FREECAD ASSEMBLY — COMPONENT RECIPES ("EL-Load-Case1")

This assembly document has 14 components, labeled P0..P13 below (a component is one placed body or linked part). 3 of them carry a construction recipe — the FreeCAD feature program that regenerates the part from scratch, quoted from this document or its linked companion documents; the rest are supplied as boundary geometry only. No exploded tour is included for this assembly.
COMPONENT P0 — geometry summary ("EL-Load-Analog"; no construction recipe available for this part):
  bounding box: 188.2 x 95.0 x 51.8 mm
  tessellated surface: 174,292 triangles
  volume: 45099 mm^3 (5% of its bounding box)
COMPONENT P1 — geometry summary ("EL-Load-Analog001"; no construction recipe available for this part):
  bounding box: 185.0 x 95.0 x 41.1 mm
  tessellated surface: 106,424 triangles
  volume: 35915 mm^3 (5% of its bounding box)
COMPONENT P2 — geometry summary ("EL-Load-PowerTest2"; no construction recipe available for this part):
  bounding box: 169.3 x 72.5 x 20.0 mm
  tessellated surface: 158,708 triangles
  volume: 24229 mm^3 (10% of its bounding box)
COMPONENT P3 — geometry summary ("EL-Load-PowerTest003"; no construction recipe available for this part):
  bounding box: 170.0 x 72.5 x 20.0 mm
  tessellated surface: 159,136 triangles
  volume: 23743 mm^3 (10% of its bounding box)
COMPONENT P4 — geometry summary ("EL-Load-PowerTest004"; no construction recipe available for this part):
  bounding box: 175.0 x 72.5 x 20.0 mm
  tessellated surface: 159,700 triangles
  volume: 25175 mm^3 (10% of its bounding box)
COMPONENT P5 — geometry summary ("EL-Load-Panel"; no construction recipe available for this part):
  bounding box: 118.0 x 45.0 x 37.4 mm
  tessellated surface: 35,930 triangles
  volume: 9733 mm^3 (5% of its bounding box)
COMPONENT P6 — geometry summary ("EL-Load-Panel003"; no construction recipe available for this part):
  bounding box: 127.0 x 53.0 x 37.4 mm
  tessellated surface: 37,466 triangles
  volume: 11392 mm^3 (5% of its bounding box)
COMPONENT P7 — geometry summary ("EL-Load-Panel005"; no construction recipe available for this part):
  bounding box: 127.0 x 53.0 x 37.4 mm
  tessellated surface: 53,262 triangles
  volume: 10742 mm^3 (4% of its bounding box)
COMPONENT P8 — geometry summary ("EL-Load-Panel006"; no construction recipe available for this part):
  bounding box: 127.0 x 53.0 x 37.4 mm
  tessellated surface: 53,262 triangles
  volume: 10742 mm^3 (4% of its bounding box)
COMPONENT P9 — geometry summary ("EL-Load-Power-MCU"; no construction recipe available for this part):
  bounding box: 179.0 x 72.5 x 19.1 mm
  tessellated surface: 186,564 triangles
  volume: 26376 mm^3 (11% of its bounding box)
COMPONENT P10 — recipe-attached ("Heatsink", modeled in this document).
Construction recipe (the document's own serialized feature program — sketch geometry with constraints, then the solid features built on it; lengths are millimeters unless a unit is written):

FEATURE [PartDesign::SubShapeBinder] Binder
  BindCopyOnChange = 0
  BindMode = 0
  ClaimChildren = false
  Context = -> Body [Binder.]
  Fuse = false
  MakeFace = true
  OffsetFill = false
  OffsetIntersection = false
  OffsetJoinType = 0
  OffsetOpenResult = false
  PartialLoad = false
  Relative = true
  Support = -> [Shape125[Face11]]
  _Version = 2
FEATURE [PartDesign::Pad] Pad
  Direction = (1,0,1e-16)
  Length = 140
  Length2 = 10
  Profile = -> Binder
  Type = 0
FEATURE [PartDesign::Body] Body  label="Heatsink"
  Group = -> [Binder,Pad]
  Origin = -> Origin067
  Tip = -> Pad
COMPONENT P11 — recipe-attached ("PCBFrame1", modeled in this document).
Construction recipe (the document's own serialized feature program — sketch geometry with constraints, then the solid features built on it; lengths are millimeters unless a unit is written):

FEATURE [Sketcher::SketchObject] Sketch
  FullyConstrained = false
  MapMode = 5
  Support = -> [XY_Plane068]
  sketch-geometry (72):
    g0: LineSegment StartX=12.25 StartY=182 StartZ=0 EndX=190.25 EndY=182 EndZ=0
    g1: LineSegment StartX=196.25 StartY=176 StartZ=0 EndX=196.25 EndY=3 EndZ=0
    g2: LineSegment StartX=190.25 StartY=-3 StartZ=0 EndX=12.25 EndY=-3 EndZ=0
    g3: LineSegment StartX=6.25 StartY=3 StartZ=0 EndX=6.25 EndY=97 EndZ=0
    g4: ArcOfCircle CenterX=190.25 CenterY=176 CenterZ=0 NormalX=0 NormalY=0 NormalZ=1 AngleXU=0 Radius=6 StartAngle=1.2e-15 EndAngle=1.5708
    g5: GeomPoint X=196.25 Y=182 Z=0
    g6: ArcOfCircle CenterX=190.25 CenterY=3 CenterZ=0 NormalX=0 NormalY=0 NormalZ=1 AngleXU=0 Radius=6 StartAngle=4.71239 EndAngle=6.28319
    g7: GeomPoint X=196.25 Y=-3 Z=0
    g8: ArcOfCircle CenterX=12.25 CenterY=176 CenterZ=0 NormalX=0 NormalY=0 NormalZ=1 AngleXU=0 Radius=6 StartAngle=1.5708 EndAngle=3.14159
    g9: GeomPoint X=6.25 Y=182 Z=0
    g10: ArcOfCircle CenterX=12.25 CenterY=3 CenterZ=0 NormalX=0 NormalY=0 NormalZ=1 AngleXU=0 Radius=6 StartAngle=3.14159 EndAngle=4.71239
    g11: GeomPoint X=6.25 Y=-3 Z=0
    g12: Circle CenterX=11 CenterY=173.498 CenterZ=0 NormalX=0 NormalY=0 NormalZ=1 AngleXU=0 Radius=1.45
    g13: Circle CenterX=11 CenterY=89.4976 CenterZ=0 NormalX=0 NormalY=0 NormalZ=1 AngleXU=0 Radius=1.45
    g14: Circle CenterX=180.742 CenterY=173.605 CenterZ=0 NormalX=0 NormalY=0 NormalZ=1 AngleXU=0 Radius=1.45
    g15: Circle CenterX=181.761 CenterY=91.0561 CenterZ=0 NormalX=0 NormalY=0 NormalZ=1 AngleXU=0 Radius=1.45
    g16: ArcOfCircle CenterX=48.25 CenterY=97.4976 CenterZ=0 NormalX=0 NormalY=0 NormalZ=1 AngleXU=0 Radius=8 StartAngle=3.14159 EndAngle=4.71239
    g17: LineSegment StartX=40.25 StartY=97.4976 StartZ=0 EndX=40.25 EndY=122 EndZ=0
    g18: ArcOfCircle CenterX=48.25 CenterY=122 CenterZ=0 NormalX=0 NormalY=0 NormalZ=1 AngleXU=0 Radius=8 StartAngle=1.5708 EndAngle=3.14159
    g19: LineSegment StartX=48.25 StartY=130 StartZ=0 EndX=168.625 EndY=130 EndZ=0
    g20: ArcOfCircle CenterX=168.625 CenterY=122 CenterZ=0 NormalX=0 NormalY=0 NormalZ=1 AngleXU=0 Radius=8 StartAngle=-9e-16 EndAngle=1.5708
    g21: LineSegment StartX=176.625 StartY=122 StartZ=0 EndX=176.625 EndY=97.4976 EndZ=0
    g22: ArcOfCircle CenterX=168.625 CenterY=97.4976 CenterZ=0 NormalX=0 NormalY=0 NormalZ=1 AngleXU=0 Radius=8 StartAngle=4.71239 EndAngle=6.28319
    g23: LineSegment StartX=168.625 StartY=89.4976 StartZ=0 EndX=48.25 EndY=89.4976 EndZ=0
    g24: GeomPoint X=40.25 Y=89.4976 Z=0
    g25: GeomPoint X=176.625 Y=130 Z=0
    g26: ArcOfCircle CenterX=23.25 CenterY=147 CenterZ=0 NormalX=0 NormalY=0 NormalZ=1 AngleXU=0 Radius=8 StartAngle=3.14159 EndAngle=4.71239
    g27: LineSegment StartX=15.25 StartY=147 StartZ=0 EndX=15.25 EndY=165.498 EndZ=0
    g28: ArcOfCircle CenterX=23.25 CenterY=165.498 CenterZ=0 NormalX=0 NormalY=0 NormalZ=1 AngleXU=0 Radius=8 StartAngle=1.5708 EndAngle=3.14159
    g29: LineSegment StartX=23.25 StartY=173.498 StartZ=0 EndX=168.564 EndY=173.498 EndZ=0
    g30: ArcOfCircle CenterX=168.564 CenterY=165.498 CenterZ=0 NormalX=0 NormalY=0 NormalZ=1 AngleXU=0 Radius=8 StartAngle=-1.8e-15 EndAngle=1.5708
    g31: LineSegment StartX=176.564 StartY=165.498 StartZ=0 EndX=176.564 EndY=147 EndZ=0
    g32: ArcOfCircle CenterX=168.564 CenterY=147 CenterZ=0 NormalX=0 NormalY=0 NormalZ=1 AngleXU=0 Radius=8 StartAngle=4.71239 EndAngle=6.28319
    g33: LineSegment StartX=168.564 StartY=139 StartZ=0 EndX=23.25 EndY=139 EndZ=0
    g34: GeomPoint X=15.25 Y=139 Z=0
    g35: GeomPoint X=176.564 Y=173.498 Z=0
    g36: LineSegment StartX=6.25 StartY=130 StartZ=0 EndX=23.25 EndY=130 EndZ=0
    g37: ArcOfCircle CenterX=23.25 CenterY=122 CenterZ=0 NormalX=0 NormalY=0 NormalZ=1 AngleXU=0 Radius=8 StartAngle=-9e-16 EndAngle=1.5708
    g38: LineSegment StartX=31.25 StartY=122 StartZ=0 EndX=31.25 EndY=105 EndZ=0
    g39: ArcOfCircle CenterX=23.25 CenterY=105 CenterZ=0 NormalX=0 NormalY=0 NormalZ=1 AngleXU=0 Radius=8 StartAngle=4.71239 EndAngle=6.28319
    g40: LineSegment StartX=23.25 StartY=97 StartZ=0 EndX=6.25 EndY=97 EndZ=0
    g41: GeomPoint X=-2.4437 Y=97 Z=0
    g42: GeomPoint X=31.25 Y=130 Z=0
    g43: LineSegment StartX=6.25 StartY=130 StartZ=0 EndX=6.25 EndY=176 EndZ=0
    g44: LineSegment StartX=15.25 StartY=147 StartZ=0 EndX=6.25 EndY=147 EndZ=0
    g45: LineSegment StartX=11 StartY=173.498 StartZ=0 EndX=16.5518 EndY=169.872 EndZ=0
    g46: LineSegment StartX=180.742 StartY=173.605 StartZ=0 EndX=175.223 EndY=169.931 EndZ=0
    g47: LineSegment StartX=181.761 StartY=91.0561 StartZ=0 EndX=175.807 EndY=93.9755 EndZ=0
    g48: LineSegment StartX=23.25 StartY=130 StartZ=0 EndX=23.25 EndY=139 EndZ=0
    g49: LineSegment StartX=48.25 StartY=130 StartZ=0 EndX=48.25 EndY=139 EndZ=0
    g50: LineSegment StartX=31.25 StartY=105 StartZ=0 EndX=40.25 EndY=105 EndZ=0
    g51: Circle CenterX=24.67 CenterY=76.67 CenterZ=0 NormalX=0 NormalY=0 NormalZ=1 AngleXU=0 Radius=1.45
    g52: Circle CenterX=24.67 CenterY=24.67 CenterZ=0 NormalX=0 NormalY=0 NormalZ=1 AngleXU=0 Radius=1.45
    g53: Circle CenterX=191.67 CenterY=24.67 CenterZ=0 NormalX=0 NormalY=0 NormalZ=1 AngleXU=0 Radius=1.45
    g54: Circle CenterX=191.67 CenterY=76.67 CenterZ=0 NormalX=0 NormalY=0 NormalZ=1 AngleXU=0 Radius=1.45
    g55: LineSegment StartX=24.67 StartY=24.67 StartZ=0 EndX=191.67 EndY=24.67 EndZ=0
    g56: LineSegment StartX=191.67 StartY=24.67 StartZ=0 EndX=191.67 EndY=76.67 EndZ=0
    g57: LineSegment StartX=191.67 StartY=76.67 StartZ=0 EndX=24.67 EndY=76.67 EndZ=0
    g58: LineSegment StartX=24.67 StartY=76.67 StartZ=0 EndX=24.67 EndY=24.67 EndZ=0
    g59: ArcOfCircle CenterX=36.92 CenterY=14 CenterZ=0 NormalX=0 NormalY=0 NormalZ=1 AngleXU=0 Radius=8 StartAngle=3.14159 EndAngle=4.71239
    g60: LineSegment StartX=28.92 StartY=14 StartZ=0 EndX=28.92 EndY=68.67 EndZ=0
    g61: ArcOfCircle CenterX=36.92 CenterY=68.67 CenterZ=0 NormalX=0 NormalY=0 NormalZ=1 AngleXU=0 Radius=8 StartAngle=1.5708 EndAngle=3.14159
    g62: LineSegment StartX=36.92 StartY=76.67 StartZ=0 EndX=179.42 EndY=76.67 EndZ=0
    g63: ArcOfCircle CenterX=179.42 CenterY=68.67 CenterZ=0 NormalX=0 NormalY=0 NormalZ=1 AngleXU=0 Radius=8 StartAngle=-9e-16 EndAngle=1.5708
    g64: LineSegment StartX=187.42 StartY=68.67 StartZ=0 EndX=187.42 EndY=14 EndZ=0
    g65: ArcOfCircle CenterX=179.42 CenterY=14 CenterZ=0 NormalX=0 NormalY=0 NormalZ=1 AngleXU=0 Radius=8 StartAngle=4.71239 EndAngle=6.28319
    g66: LineSegment StartX=179.42 StartY=6 StartZ=0 EndX=36.92 EndY=6 EndZ=0
    g67: GeomPoint X=28.92 Y=6 Z=0
    g68: GeomPoint X=187.42 Y=76.67 Z=0
    g69: LineSegment StartX=36.92 StartY=6 StartZ=0 EndX=36.92 EndY=-3 EndZ=0
    g70: LineSegment StartX=24.67 StartY=76.67 StartZ=0 EndX=30.2218 EndY=73.0443 EndZ=0
    g71: LineSegment StartX=191.67 StartY=76.67 StartZ=0 EndX=186.118 EndY=73.0443 EndZ=0
  constraints (180):
    c: Horizontal(g0)
    c: Horizontal(g2)
    c: Vertical(g1)
    c: Vertical(g3)
    c: DistanceY(g11,g9) = 185
    c: DistanceY(g11,g-1) = 3
    c: DistanceX(g-1,g11) = 6.25
    c: DistanceX(g9,g5) = 190
    c: PointOnObject(g5,g0)
    c: PointOnObject(g5,g1)
    c: Tangent(g0,g4) = 1.5708
    c: Tangent(g1,g4) = 1.5708
    c: PointOnObject(g7,g1)
    c: PointOnObject(g7,g2)
    c: Tangent(g1,g6) = 1.5708
    c: Tangent(g2,g6) = 1.5708
    c: PointOnObject(g9,g0)
    c: PointOnObject(g9,g3)
    c: Tangent(g0,g8) = 1.5708
    c: PointOnObject(g11,g2)
    c: PointOnObject(g11,g3)
    c: Tangent(g2,g10) = 1.5708
    c: Tangent(g3,g10) = 1.5708
    c: Equal(g10,g8)
    c: Equal(g8,g4)
    c: Equal(g4,g6)
    c: Radius(g4) = 6
    c: Equal(g15,g14)
    c: Equal(g14,g12)
    c: Equal(g12,g13)
    c: Vertical(g12,g13)
    c: Diameter(g15) = 2.9
    c: DistanceX(g15) = 181.761
    c: DistanceY(g15) = 91.0561
    c: DistanceX(g14) = 180.742
    c: DistanceY(g14) = 173.605
    c: DistanceX(g12) = 11
    c: DistanceY(g12) = 173.498
    c: DistanceY(g13,g12) = 84
    c: Tangent(g16,g17) = 1.5708
    c: Tangent(g17,g18) = 1.5708
    c: Tangent(g18,g19) = 1.5708
    c: Tangent(g19,g20) = 1.5708
    c: Tangent(g20,g21) = 1.5708
    c: Tangent(g21,g22) = 1.5708
    c: Tangent(g22,g23) = 1.5708
    c: Tangent(g23,g16) = 1.5708
    c: Horizontal(g19)
    c: Horizontal(g23)
    c: Vertical(g17)
    c: Vertical(g21)
    c: Equal(g16,g18)
    c: Equal(g18,g20)
    c: Equal(g20,g22)
    c: PointOnObject(g24,g17)
    c: PointOnObject(g24,g23)
    c: PointOnObject(g25,g19)
    c: PointOnObject(g25,g21)
    c: Tangent(g26,g27) = 1.5708
    c: Tangent(g27,g28) = 1.5708
    c: Tangent(g28,g29) = 1.5708
    c: Tangent(g29,g30) = 1.5708
    c: Tangent(g30,g31) = 1.5708
    c: Tangent(g31,g32) = 1.5708
    c: Tangent(g32,g33) = 1.5708
    c: Tangent(g33,g26) = 1.5708
    c: Horizontal(g29)
    c: Horizontal(g33)
    c: Vertical(g27)
    c: Vertical(g31)
    c: Equal(g26,g28)
    c: Equal(g28,g30)
    c: Equal(g30,g32)
    c: PointOnObject(g34,g27)
    c: PointOnObject(g34,g33)
    c: PointOnObject(g35,g29)
    c: PointOnObject(g35,g31)
    c: Tangent(g36,g37) = 1.5708
    c: Tangent(g37,g38) = 1.5708
    c: Tangent(g38,g39) = 1.5708
    c: Tangent(g39,g40) = 1.5708
    c: Horizontal(g36)
    c: Horizontal(g40)
    c: Vertical(g38)
    c: Equal(g37,g39)
    c: PointOnObject(g41,g40)
    c: PointOnObject(g42,g36)
    c: PointOnObject(g42,g38)
    c: Coincident(g3,g40)
    c: Coincident(g43,g36)
    c: Equal(g18,g37)
    c: Equal(g37,g26)
    c: Horizontal(g28,g12)
    c: Coincident(g44,g26)
    c: Horizontal(g44)
    c: Coincident(g45,g12)
    c: PointOnObject(g45,g28)
    c: Perpendicular(g28,g45)
    c: Coincident(g46,g14)
    c: PointOnObject(g46,g30)
    c: Perpendicular(g30,g46)
    c: Equal(g46,g45)
    c: Perpendicular(g22,g47)
    c: Equal(g47,g46)
    c: PointOnObject(g47,g22)
    c: Coincident(g47,g15)
    c: Vertical(g43)
    c: PointOnObject(g44,g43)
    c: Radius(g26) = 8
    c: Vertical(g36,g3)
    c: DistanceY(g36,g0) = 52
    c: DistanceY(g3,g36) = 33
    c: Coincident(g48,g36)
    c: Coincident(g48,g26)
    c: Vertical(g48)
    c: Equal(g48,g44)
    c: Horizontal(g16,g13)
    c: Coincident(g49,g18)
    c: PointOnObject(g49,g33)
    c: Vertical(g49)
    c: Coincident(g50,g38)
    c: PointOnObject(g50,g17)
    c: Horizontal(g50)
    c: Equal(g49,g48)
    c: Equal(g50,g48)
    c: DistanceX(g3,g38) = 25
    c: Tangent(g43,g8) = 1.5708
    c: Equal(g54,g53)
    c: Equal(g53,g52)
    c: Equal(g52,g51)
    c: Equal(g51,g15)
    c: Coincident(g55,g56)
    c: Coincident(g56,g57)
    c: Coincident(g57,g58)
    c: Coincident(g58,g55)
    c: Horizontal(g55)
    c: Horizontal(g57)
    c: Vertical(g56)
    c: Vertical(g58)
    c: Coincident(g52,g55)
    c: Coincident(g54,g56)
    c: Coincident(g55,g53)
    c: Coincident(g57,g51)
    c: DistanceY(g58,g58) = 52
    c: DistanceX(g52,g53) = 167
    c: DistanceX(g52) = 24.67
    c: DistanceY(g52) = 24.67
    c: Tangent(g59,g60) = 1.5708
    c: Tangent(g60,g61) = 1.5708
    c: Tangent(g61,g62) = 1.5708
    c: Tangent(g62,g63) = 1.5708
    c: Tangent(g63,g64) = 1.5708
    c: Tangent(g64,g65) = 1.5708
    c: Tangent(g65,g66) = 1.5708
    c: Tangent(g66,g59) = 1.5708
    c: Horizontal(g62)
    c: Horizontal(g66)
    c: Vertical(g60)
    c: Vertical(g64)
    c: Equal(g59,g61)
    c: Equal(g61,g63)
    c: Equal(g63,g65)
    c: PointOnObject(g67,g60)
    c: PointOnObject(g67,g66)
    c: PointOnObject(g68,g62)
    c: PointOnObject(g68,g64)
    c: Equal(g61,g16)
    c: Horizontal(g61,g51)
    c: Coincident(g69,g59)
    c: PointOnObject(g69,g2)
    c: Vertical(g69)
    c: Coincident(g70,g51)
    c: PointOnObject(g70,g61)
    c: Perpendicular(g61,g70)
    c: Equal(g69,g50)
    c: Equal(g70,g45)
    c: Coincident(g71,g54)
    c: PointOnObject(g71,g63)
    c: Perpendicular(g63,g71)
    c: Equal(g71,g70)
FEATURE [PartDesign::Pad] Pad001
  Direction = (0,0,1)
  Length = 1.6
  Length2 = 10
  Profile = -> Sketch
  ReferenceAxis = -> Sketch [N_Axis]
  Reversed = true
  Type = 0
FEATURE [Sketcher::SketchObject] Sketch001
  ExternalGeometry = -> [Pad001]
  FullyConstrained = true
  MapMode = 5
  Support = -> [XY_Plane068]
  sketch-geometry (12):
    g0: Circle CenterX=24.67 CenterY=24.67 CenterZ=0 NormalX=0 NormalY=0 NormalZ=1 AngleXU=0 Radius=1.45
    g1: Circle CenterX=191.67 CenterY=76.67 CenterZ=0 NormalX=0 NormalY=0 NormalZ=1 AngleXU=0 Radius=1.45
    g2: Circle CenterX=191.67 CenterY=24.67 CenterZ=0 NormalX=0 NormalY=0 NormalZ=1 AngleXU=0 Radius=1.45
    g3: ArcOfCircle CenterX=24.67 CenterY=76.67 CenterZ=0 NormalX=0 NormalY=0 NormalZ=1 AngleXU=0 Radius=4.25 StartAngle=-4.361e-13 EndAngle=3.14159
    g4: ArcOfCircle CenterX=24.67 CenterY=6 CenterZ=0 NormalX=0 NormalY=0 NormalZ=1 AngleXU=0 Radius=4.25 StartAngle=3.14159 EndAngle=6.28319
    g5: LineSegment StartX=20.42 StartY=76.67 StartZ=0 EndX=20.42 EndY=6 EndZ=0
    g6: LineSegment StartX=28.92 StartY=6 StartZ=0 EndX=28.92 EndY=76.67 EndZ=0
    g7: ArcOfCircle CenterX=191.835 CenterY=76.67 CenterZ=0 NormalX=0 NormalY=0 NormalZ=1 AngleXU=0 Radius=4.415 StartAngle=-3.162e-13 EndAngle=3.14159
    g8: ArcOfCircle CenterX=191.835 CenterY=6 CenterZ=0 NormalX=0 NormalY=0 NormalZ=1 AngleXU=0 Radius=4.415 StartAngle=3.14159 EndAngle=6.28319
    g9: LineSegment StartX=187.42 StartY=76.67 StartZ=0 EndX=187.42 EndY=6 EndZ=0
    g10: LineSegment StartX=196.25 StartY=6 StartZ=0 EndX=196.25 EndY=76.67 EndZ=0
    g11: Circle CenterX=24.67 CenterY=76.67 CenterZ=0 NormalX=0 NormalY=0 NormalZ=1 AngleXU=0 Radius=1.45
  constraints (27):
    c: Coincident(g0,g-3)
    c: Coincident(g1,g-4)
    c: Coincident(g2,g-5)
    c: Equal(g2,g-5)
    c: Equal(g1,g-4)
    c: Equal(g0,g-3)
    c: Tangent(g3,g5) = -1.5708
    c: Tangent(g5,g4) = -1.5708
    c: Tangent(g4,g6) = -1.5708
    c: Tangent(g6,g3) = -1.5708
    c: Equal(g3,g4)
    c: Vertical(g5)
    c: PointOnObject(g-6,g6)
    c: Coincident(g3,g-9)
    c: Horizontal(g4,g-7)
    c: Tangent(g9,g7) = -1.5708
    c: Tangent(g7,g10) = -1.5708
    c: Equal(g7,g8)
    c: Tangent(g9,g8) = -1.5708
    c: Tangent(g8,g10) = -1.5708
    c: Vertical(g8,g7)
    c: Horizontal(g8,g-7)
    c: PointOnObject(g7,g-10)
    c: PointOnObject(g-8,g9)
    c: Horizontal(g7,g1)
    c: Coincident(g11,g3)
    c: Equal(g11,g-9)
FEATURE [PartDesign::Pad] Pad002
  BaseFeature = -> Pad001
  Direction = (0,0,1)
  Length = 13.75
  Length2 = 10
  Profile = -> Sketch001
  ReferenceAxis = -> Sketch001 [N_Axis]
  Type = 0
FEATURE [Sketcher::SketchObject] Sketch002
  FullyConstrained = true
  MapMode = 5
  Placement = pos=(196.25,1.2619e-12,0) rot=(0.57735,0.57735,0.57735;2.0944rad)
  Support = -> [Pad002]
  sketch-geometry (10):
    g0: ArcOfCircle CenterX=31 CenterY=19 CenterZ=0 NormalX=0 NormalY=0 NormalZ=1 AngleXU=0 Radius=3 StartAngle=1.5708 EndAngle=3.14159
    g1: LineSegment StartX=31 StartY=22 StartZ=0 EndX=61 EndY=22 EndZ=0
    g2: ArcOfCircle CenterX=61 CenterY=19 CenterZ=0 NormalX=0 NormalY=0 NormalZ=1 AngleXU=0 Radius=3 StartAngle=-2.71463e-11 EndAngle=1.5708
    g3: LineSegment StartX=64 StartY=19 StartZ=0 EndX=64 EndY=9 EndZ=0
    g4: ArcOfCircle CenterX=61 CenterY=9 CenterZ=0 NormalX=0 NormalY=0 NormalZ=1 AngleXU=0 Radius=3 StartAngle=4.71239 EndAngle=6.28319
    g5: LineSegment StartX=61 StartY=6 StartZ=0 EndX=31 EndY=6 EndZ=0
    g6: ArcOfCircle CenterX=31 CenterY=9 CenterZ=0 NormalX=0 NormalY=0 NormalZ=1 AngleXU=0 Radius=3 StartAngle=3.14159 EndAngle=4.71239
    g7: LineSegment StartX=28 StartY=9 StartZ=0 EndX=28 EndY=19 EndZ=0
    g8: GeomPoint X=28 Y=22 Z=0
    g9: GeomPoint X=64 Y=6 Z=0
  constraints (24):
    c: Tangent(g0,g1) = 1.5708
    c: Tangent(g1,g2) = 1.5708
    c: Tangent(g2,g3) = 1.5708
    c: Tangent(g3,g4) = 1.5708
    c: Tangent(g4,g5) = 1.5708
    c: Tangent(g5,g6) = 1.5708
    c: Tangent(g6,g7) = 1.5708
    c: Tangent(g7,g0) = 1.5708
    c: Horizontal(g1)
    c: Horizontal(g5)
    c: Vertical(g3)
    c: Vertical(g7)
    c: Equal(g0,g2)
    c: Equal(g2,g4)
    c: Equal(g4,g6)
    c: PointOnObject(g8,g1)
    c: PointOnObject(g8,g7)
    c: PointOnObject(g9,g3)
    c: PointOnObject(g9,g5)
    c: Radius(g4) = 3
    c: DistanceX(g6,g3) = 36
    c: DistanceY(g-1,g5) = 6
    c: DistanceX(g6) = 28
    c: DistanceY(g3,g2) = 10
FEATURE [PartDesign::Pocket] Pocket
  BaseFeature = -> Pad002
  Direction = (-1,-6.3e-15,-1e-16)
  Length = 15
  Length2 = 5
  Profile = -> Sketch002
  ReferenceAxis = -> Sketch002 [N_Axis]
  Type = 0
FEATURE [Sketcher::SketchObject] Sketch003
  AttachmentOffset = pos=(0,0,-0.1) rot=(0,0,1;0rad)
  ExternalGeometry = -> [Pocket]
  FullyConstrained = true
  MapMode = 5
  Placement = pos=(0,0,-0.1) rot=(0,0,1;0rad)
  Support = -> [XY_Plane068]
  sketch-geometry (22):
    g0: ArcOfCircle CenterX=181.761 CenterY=91.0561 CenterZ=0 NormalX=0 NormalY=0 NormalZ=1 AngleXU=0 Radius=4.54989 StartAngle=0.603158 EndAngle=3.74475
    g1: ArcOfCircle CenterX=191.67 CenterY=76.67 CenterZ=0 NormalX=0 NormalY=0 NormalZ=1 AngleXU=0 Radius=4.54989 StartAngle=3.74475 EndAngle=6.88634
    g2: LineSegment StartX=178.014 StartY=88.4752 StartZ=0 EndX=187.923 EndY=74.0891 EndZ=0
    g3: LineSegment StartX=195.417 StartY=79.2509 StartZ=0 EndX=185.508 EndY=93.637 EndZ=0
    g4: ArcOfCircle CenterX=11 CenterY=89.4976 CenterZ=0 NormalX=0 NormalY=0 NormalZ=1 AngleXU=0 Radius=4.25 StartAngle=0.817178 EndAngle=3.95877
    g5: ArcOfCircle CenterX=24.67 CenterY=76.67 CenterZ=0 NormalX=0 NormalY=0 NormalZ=1 AngleXU=0 Radius=4.25 StartAngle=3.95877 EndAngle=7.10036
    g6: LineSegment StartX=8.0918 StartY=86.3984 StartZ=0 EndX=21.7618 EndY=73.5708 EndZ=0
    g7: LineSegment StartX=27.5782 StartY=79.7692 StartZ=0 EndX=13.9082 EndY=92.5968 EndZ=0
    g8: Circle CenterX=191.67 CenterY=76.67 CenterZ=0 NormalX=0 NormalY=0 NormalZ=1 AngleXU=0 Radius=1.45
    g9: Circle CenterX=181.761 CenterY=91.0561 CenterZ=0 NormalX=0 NormalY=0 NormalZ=1 AngleXU=0 Radius=1.45
    g10: Circle CenterX=24.67 CenterY=76.67 CenterZ=0 NormalX=0 NormalY=0 NormalZ=1 AngleXU=0 Radius=1.45
    g11: Circle CenterX=11 CenterY=89.4976 CenterZ=0 NormalX=0 NormalY=0 NormalZ=1 AngleXU=0 Radius=1.45
    g12: ArcOfCircle CenterX=11 CenterY=173.498 CenterZ=0 NormalX=0 NormalY=0 NormalZ=1 AngleXU=0 Radius=4.25 StartAngle=-4.035e-12 EndAngle=3.14159
    g13: ArcOfCircle CenterX=11 CenterY=165.498 CenterZ=0 NormalX=0 NormalY=0 NormalZ=1 AngleXU=0 Radius=4.25 StartAngle=3.14159 EndAngle=6.28319
    g14: LineSegment StartX=6.75 StartY=173.498 StartZ=0 EndX=6.75 EndY=165.498 EndZ=0
    g15: LineSegment StartX=15.25 StartY=165.498 StartZ=0 EndX=15.25 EndY=173.498 EndZ=0
    g16: Circle CenterX=11 CenterY=173.498 CenterZ=0 NormalX=0 NormalY=0 NormalZ=1 AngleXU=0 Radius=1.45
    g17: ArcOfCircle CenterX=180.742 CenterY=173.605 CenterZ=0 NormalX=0 NormalY=0 NormalZ=1 AngleXU=0 Radius=4.54989 StartAngle=1.5708 EndAngle=4.71239
    g18: ArcOfCircle CenterX=191.7 CenterY=173.605 CenterZ=0 NormalX=0 NormalY=0 NormalZ=1 AngleXU=0 Radius=4.54989 StartAngle=4.71239 EndAngle=7.85398
    g19: LineSegment StartX=180.742 StartY=169.055 StartZ=0 EndX=191.7 EndY=169.055 EndZ=0
    g20: LineSegment StartX=191.7 StartY=178.155 StartZ=0 EndX=180.742 EndY=178.155 EndZ=0
    g21: Circle CenterX=180.742 CenterY=173.605 CenterZ=0 NormalX=0 NormalY=0 NormalZ=1 AngleXU=0 Radius=1.45
  constraints (45):
    c: Tangent(g0,g2) = -1.5708
    c: Tangent(g2,g1) = -1.5708
    c: Tangent(g1,g3) = -1.5708
    c: Tangent(g3,g0) = -1.5708
    c: Equal(g0,g1)
    c: Tangent(g4,g6) = -1.5708
    c: Tangent(g6,g5) = -1.5708
    c: Tangent(g5,g7) = -1.5708
    c: Tangent(g7,g4) = -1.5708
    c: Equal(g4,g5)
    c: Coincident(g4,g-5)
    c: Coincident(g0,g-3)
    c: Coincident(g-7,g1)
    c: PointOnObject(g1,g-13)
    c: Coincident(g8,g1)
    c: Equal(g-7,g8)
    c: Coincident(g9,g0)
    c: Equal(g-3,g9)
    c: Coincident(g-4,g5)
    c: Coincident(g10,g5)
    c: Coincident(g11,g4)
    c: Equal(g-5,g11)
    c: Equal(g-4,g10)
    c: PointOnObject(g5,g-14)
    c: Tangent(g12,g14) = -1.5708
    c: Tangent(g14,g13) = -1.5708
    c: Tangent(g13,g15) = -1.5708
    c: Tangent(g15,g12) = -1.5708
    c: Equal(g12,g13)
    c: Coincident(g12,g-15)
    c: Vertical(g14)
    c: Coincident(g13,g-12)
    c: Coincident(g16,g12)
    c: Equal(g16,g-15)
    c: Tangent(g17,g19) = -1.5708
    c: Tangent(g19,g18) = -1.5708
    c: Tangent(g18,g20) = -1.5708
    c: Tangent(g20,g17) = -1.5708
    c: Equal(g17,g18)
    c: Coincident(g17,g-6)
    c: Horizontal(g19)
    c: Coincident(g21,g17)
    c: Equal(g21,g-6)
    c: Tangent(g-11,g18)
    c: Equal(g0,g17)
FEATURE [PartDesign::Pad] Pad003
  BaseFeature = -> Pocket
  Direction = (0,0,1)
  Length = 3.4
  Length2 = 10
  Profile = -> Sketch003
  ReferenceAxis = -> Sketch003 [N_Axis]
  Type = 0
FEATURE [Sketcher::SketchObject] Sketch004
  FullyConstrained = true
  MapMode = 5
  Support = -> [XY_Plane068]
  sketch-geometry (20):
    g0: ArcOfCircle CenterX=75.7237 CenterY=139.855 CenterZ=0 NormalX=0 NormalY=0 NormalZ=1 AngleXU=0 Radius=1 StartAngle=1.5708 EndAngle=3.14159
    g1: LineSegment StartX=75.7237 StartY=140.855 StartZ=0 EndX=91.4237 EndY=140.855 EndZ=0
    g2: ArcOfCircle CenterX=91.4237 CenterY=139.855 CenterZ=0 NormalX=0 NormalY=0 NormalZ=1 AngleXU=0 Radius=1 StartAngle=9.8e-15 EndAngle=1.5708
    g3: LineSegment StartX=92.4237 StartY=139.855 StartZ=0 EndX=92.4237 EndY=134.855 EndZ=0
    g4: ArcOfCircle CenterX=91.4237 CenterY=134.855 CenterZ=0 NormalX=0 NormalY=0 NormalZ=1 AngleXU=0 Radius=1 StartAngle=4.71239 EndAngle=6.28319
    g5: LineSegment StartX=91.4237 StartY=133.855 StartZ=0 EndX=75.7237 EndY=133.855 EndZ=0
    g6: ArcOfCircle CenterX=75.7237 CenterY=134.855 CenterZ=0 NormalX=0 NormalY=0 NormalZ=1 AngleXU=0 Radius=1 StartAngle=3.14159 EndAngle=4.71239
    g7: LineSegment StartX=74.7237 StartY=134.855 StartZ=0 EndX=74.7237 EndY=139.855 EndZ=0
    g8: GeomPoint X=74.7237 Y=140.855 Z=0
    g9: GeomPoint X=92.4237 Y=133.855 Z=0
    g10: ArcOfCircle CenterX=129.924 CenterY=139.855 CenterZ=0 NormalX=0 NormalY=0 NormalZ=1 AngleXU=0 Radius=1 StartAngle=1.5708 EndAngle=3.14159
    g11: LineSegment StartX=129.924 StartY=140.855 StartZ=0 EndX=145.624 EndY=140.855 EndZ=0
    g12: ArcOfCircle CenterX=145.624 CenterY=139.855 CenterZ=0 NormalX=0 NormalY=0 NormalZ=1 AngleXU=0 Radius=1 StartAngle=-8.9e-15 EndAngle=1.5708
    g13: LineSegment StartX=146.624 StartY=139.855 StartZ=0 EndX=146.624 EndY=134.855 EndZ=0
    g14: ArcOfCircle CenterX=145.624 CenterY=134.855 CenterZ=0 NormalX=0 NormalY=0 NormalZ=1 AngleXU=0 Radius=1 StartAngle=4.71239 EndAngle=6.28319
    g15: LineSegment StartX=145.624 StartY=133.855 StartZ=0 EndX=129.924 EndY=133.855 EndZ=0
    g16: ArcOfCircle CenterX=129.924 CenterY=134.855 CenterZ=0 NormalX=0 NormalY=0 NormalZ=1 AngleXU=0 Radius=1 StartAngle=3.14159 EndAngle=4.71239
    g17: LineSegment StartX=128.924 StartY=134.855 StartZ=0 EndX=128.924 EndY=139.855 EndZ=0
    g18: GeomPoint X=128.924 Y=140.855 Z=0
    g19: GeomPoint X=146.624 Y=133.855 Z=0
  constraints (48):
    c: Tangent(g0,g1) = 1.5708
    c: Tangent(g1,g2) = 1.5708
    c: Tangent(g2,g3) = 1.5708
    c: Tangent(g3,g4) = 1.5708
    c: Tangent(g4,g5) = 1.5708
    c: Tangent(g5,g6) = 1.5708
    c: Tangent(g6,g7) = 1.5708
    c: Tangent(g7,g0) = 1.5708
    c: Horizontal(g1)
    c: Horizontal(g5)
    c: Vertical(g3)
    c: Vertical(g7)
    c: Equal(g0,g2)
    c: Equal(g2,g4)
    c: Equal(g4,g6)
    c: PointOnObject(g8,g1)
    c: PointOnObject(g8,g7)
    c: PointOnObject(g9,g3)
    c: PointOnObject(g9,g5)
    c: Tangent(g10,g11) = 1.5708
    c: Tangent(g11,g12) = 1.5708
    c: Tangent(g12,g13) = 1.5708
    c: Tangent(g13,g14) = 1.5708
    c: Tangent(g14,g15) = 1.5708
    c: Tangent(g15,g16) = 1.5708
    c: Tangent(g16,g17) = 1.5708
    c: Tangent(g17,g10) = 1.5708
    c: Horizontal(g11)
    c: Horizontal(g15)
    c: Vertical(g13)
    c: Vertical(g17)
    c: Equal(g10,g12)
    c: Equal(g12,g14)
    c: Equal(g14,g16)
    c: PointOnObject(g18,g11)
    c: PointOnObject(g18,g17)
    c: PointOnObject(g19,g13)
    c: PointOnObject(g19,g15)
    c: Horizontal(g4,g15)
    c: Equal(g1,g11)
    c: Equal(g2,g10)
    c: Horizontal(g10,g1)
    c: DistanceX(g5) = 75.7237
    c: DistanceY(g5) = 133.855
    c: DistanceX(g5,g5) = 15.7
    c: DistanceY(g3,g3) = 5
    c: Radius(g2) = 1
    c: DistanceX(g4,g15) = 38.5
FEATURE [PartDesign::Pocket] Pocket001
  BaseFeature = -> Pad003
  Direction = (0,0,-1)
  Length = 5
  Length2 = 5
  Profile = -> Sketch004
  ReferenceAxis = -> Sketch004 [N_Axis]
  Type = 0
FEATURE [Sketcher::SketchObject] Sketch008
  ExternalGeometry = -> [Pocket001]
  FullyConstrained = true
  MapMode = 5
  Support = -> [XY_Plane068]
  sketch-geometry (6):
    g0: ArcOfCircle CenterX=26.42 CenterY=3 CenterZ=0 NormalX=0 NormalY=0 NormalZ=1 AngleXU=0 Radius=6 StartAngle=3.14159 EndAngle=4.71239
    g1: LineSegment StartX=20.42 StartY=3 StartZ=0 EndX=20.42 EndY=84 EndZ=0
    g2: LineSegment StartX=20.42 StartY=84 StartZ=0 EndX=-9.58 EndY=84 EndZ=0
    g3: LineSegment StartX=-9.58 StartY=84 StartZ=0 EndX=-9.58 EndY=-33 EndZ=0
    g4: LineSegment StartX=-9.58 StartY=-33 StartZ=0 EndX=26.42 EndY=-33 EndZ=0
    g5: LineSegment StartX=26.42 StartY=-33 StartZ=0 EndX=26.42 EndY=-3 EndZ=0
  constraints (18):
    c: Equal(g0,g-3)
    c: Vertical(g1)
    c: Coincident(g2,g1)
    c: Horizontal(g2)
    c: Coincident(g3,g2)
    c: Vertical(g3)
    c: Coincident(g4,g3)
    c: Horizontal(g4)
    c: Coincident(g5,g4)
    c: Coincident(g5,g0)
    c: Vertical(g5)
    c: Tangent(g0,g1) = 1.5708
    c: Horizontal(g-3,g0)
    c: Vertical(g0,g-4)
    c: Perpendicular(g0,g5)
    c: Equal(g2,g5)
    c: Distance(g5) = 30
    c: DistanceY(g0,g1) = 87
FEATURE [PartDesign::Pocket] Pocket002
  BaseFeature = -> Pocket001
  Direction = (0,0,-1)
  Length = 20
  Length2 = 5
  Midplane = true
  Profile = -> Sketch008
  ReferenceAxis = -> Sketch008 [N_Axis]
  Type = 0
FEATURE [PartDesign::Body] Body001  label="PCBFrame1"
  Group = -> [Sketch,Pad001,Sketch001,Pad002,Sketch002,Pocket,Sketch003,Pad003,Sketch004,Pocket001,Sketch008,Pocket002]
  Origin = -> Origin068
  Placement = pos=(0,0,-3.4) rot=(0,0,1;0rad)
  Tip = -> Pocket002
COMPONENT P12 — recipe-attached ("Front Panel", modeled in this document).
Construction recipe (the document's own serialized feature program — sketch geometry with constraints, then the solid features built on it; lengths are millimeters unless a unit is written):

FEATURE [PartDesign::SubShapeBinder] Binder001
  BindCopyOnChange = 0
  BindMode = 0
  ClaimChildren = false
  Context = -> Body002 [Binder001.]
  Fuse = false
  MakeFace = true
  OffsetFill = false
  OffsetIntersection = false
  OffsetJoinType = 0
  OffsetOpenResult = false
  PartialLoad = false
  Relative = true
  Support = -> [_455U2201[Part__Feature021.]]
  _Version = 2
FEATURE [Sketcher::SketchObject] Sketch006  label="Fan"
  AttachmentOffset = pos=(55,-105,0) rot=(0,0,1;0.785398rad)
  FullyConstrained = true
  MapMode = 5
  Placement = pos=(3.55e-14,55,-105) rot=(0.678598,0.281085,0.678598;2.59356rad)
  Support = -> [YZ_Plane069]
  sketch-geometry (11):
    g0: LineSegment StartX=173.5 StartY=33.6 StartZ=0 EndX=141.5 EndY=33.6 EndZ=0
    g1: LineSegment StartX=141.5 StartY=33.6 StartZ=0 EndX=141.5 EndY=1.6 EndZ=0
    g2: LineSegment StartX=141.5 StartY=1.6 StartZ=0 EndX=173.5 EndY=1.6 EndZ=0
    g3: LineSegment StartX=173.5 StartY=1.6 StartZ=0 EndX=173.5 EndY=33.6 EndZ=0
    g4: Circle CenterX=173.5 CenterY=33.6 CenterZ=0 NormalX=0 NormalY=0 NormalZ=1 AngleXU=0 Radius=2
    g5: Circle CenterX=141.5 CenterY=33.6 CenterZ=0 NormalX=0 NormalY=0 NormalZ=1 AngleXU=0 Radius=2
    g6: Circle CenterX=141.5 CenterY=1.6 CenterZ=0 NormalX=0 NormalY=0 NormalZ=1 AngleXU=0 Radius=2
    g7: Circle CenterX=173.5 CenterY=1.6 CenterZ=0 NormalX=0 NormalY=0 NormalZ=1 AngleXU=0 Radius=2
    g8: Circle CenterX=157.5 CenterY=17.6 CenterZ=0 NormalX=0 NormalY=0 NormalZ=1 AngleXU=0 Radius=19.5
    g9: LineSegment StartX=157.5 StartY=17.6 StartZ=0 EndX=157.5 EndY=33.6 EndZ=0
    g10: LineSegment StartX=157.5 StartY=17.6 StartZ=0 EndX=157.5 EndY=1.6 EndZ=0
  constraints (28):
    c: Coincident(g0,g1)
    c: Coincident(g1,g2)
    c: Coincident(g2,g3)
    c: Coincident(g3,g0)
    c: Horizontal(g0)
    c: Horizontal(g2)
    c: Vertical(g1)
    c: Vertical(g3)
    c: Equal(g1,g2)
    c: Coincident(g4,g0)
    c: Coincident(g5,g0)
    c: Coincident(g6,g1)
    c: Coincident(g7,g2)
    c: Equal(g7,g6)
    c: Equal(g6,g5)
    c: Equal(g5,g4)
    c: Diameter(g6) = 4
    c: Coincident(g9,g8)
    c: Vertical(g9)
    c: Symmetric(g5,g4,g9)
    c: Diameter(g8) = 39
    c: Coincident(g10,g8)
    c: PointOnObject(g10,g2)
    c: Vertical(g10)
    c: Equal(g10,g9)
    c: Distance(g0) = 32
    c: DistanceX(g7) = 173.5
    c: DistanceY(g7) = 1.6
FEATURE [Sketcher::SketchObject] Sketch007  label="Panel"
  ExternalGeometry = -> [Binder001]
  FullyConstrained = true
  MapMode = 5
  Placement = pos=(0,0,0) rot=(0.57735,0.57735,0.57735;2.0944rad)
  Support = -> [YZ_Plane069]
  sketch-geometry (18):
    g0: ArcOfCircle CenterX=181.1 CenterY=49.2 CenterZ=0 NormalX=0 NormalY=0 NormalZ=1 AngleXU=0 Radius=3.9 StartAngle=-8.429e-13 EndAngle=1.5708
    g1: LineSegment StartX=185 StartY=49.2 StartZ=0 EndX=185 EndY=-9 EndZ=0
    g2: ArcOfCircle CenterX=181.1 CenterY=-9 CenterZ=0 NormalX=0 NormalY=0 NormalZ=1 AngleXU=0 Radius=3.9 StartAngle=4.71239 EndAngle=6.28319
    g3: LineSegment StartX=181.1 StartY=-12.9 StartZ=0 EndX=-2.1 EndY=-12.9 EndZ=0
    g4: ArcOfCircle CenterX=-2.1 CenterY=-9 CenterZ=0 NormalX=0 NormalY=0 NormalZ=1 AngleXU=0 Radius=3.9 StartAngle=3.14159 EndAngle=4.71239
    g5: LineSegment StartX=-6 StartY=-9 StartZ=0 EndX=-6 EndY=49.2 EndZ=0
    g6: ArcOfCircle CenterX=-2.1 CenterY=49.2 CenterZ=0 NormalX=0 NormalY=0 NormalZ=1 AngleXU=0 Radius=3.9 StartAngle=1.5708 EndAngle=3.14159
    g7: LineSegment StartX=-2.1 StartY=53.1 StartZ=0 EndX=181.1 EndY=53.1 EndZ=0
    g8: GeomPoint X=185 Y=53.1 Z=0
    g9: GeomPoint X=-6 Y=-12.9 Z=0
    g10: Circle CenterX=180.25 CenterY=49.11 CenterZ=0 NormalX=0 NormalY=0 NormalZ=1 AngleXU=0 Radius=2.1
    g11: Circle CenterX=180.25 CenterY=-8.91 CenterZ=0 NormalX=0 NormalY=0 NormalZ=1 AngleXU=0 Radius=2.1
    g12: Circle CenterX=-1.25 CenterY=-8.91 CenterZ=0 NormalX=0 NormalY=0 NormalZ=1 AngleXU=0 Radius=2.1
    g13: Circle CenterX=-1.25 CenterY=49.11 CenterZ=0 NormalX=0 NormalY=0 NormalZ=1 AngleXU=0 Radius=2.1
    g14: LineSegment StartX=-1.25 StartY=49.11 StartZ=0 EndX=180.25 EndY=49.11 EndZ=0
    g15: LineSegment StartX=180.25 StartY=49.11 StartZ=0 EndX=180.25 EndY=-8.91 EndZ=0
    g16: LineSegment StartX=180.25 StartY=-8.91 StartZ=0 EndX=-1.25 EndY=-8.91 EndZ=0
    g17: LineSegment StartX=-1.25 StartY=-8.91 StartZ=0 EndX=-1.25 EndY=49.11 EndZ=0
  constraints (42):
    c: Tangent(g0,g1) = 1.5708
    c: Tangent(g1,g2) = 1.5708
    c: Tangent(g2,g3) = 1.5708
    c: Tangent(g3,g4) = 1.5708
    c: Tangent(g4,g5) = 1.5708
    c: Tangent(g5,g6) = 1.5708
    c: Tangent(g6,g7) = 1.5708
    c: Tangent(g7,g0) = 1.5708
    c: Horizontal(g3)
    c: Horizontal(g7)
    c: Vertical(g1)
    c: Vertical(g5)
    c: Equal(g0,g2)
    c: Equal(g2,g4)
    c: Equal(g4,g6)
    c: PointOnObject(g8,g1)
    c: PointOnObject(g8,g7)
    c: PointOnObject(g9,g3)
    c: PointOnObject(g9,g5)
    c: Coincident(g4,g-6)
    c: Coincident(g0,g-4)
    c: PointOnObject(g2,g-5)
    c: Coincident(g14,g15)
    c: Coincident(g15,g16)
    c: Coincident(g16,g17)
    c: Coincident(g17,g14)
    c: Horizontal(g14)
    c: Horizontal(g16)
    c: Vertical(g15)
    c: Vertical(g17)
    c: Coincident(g11,g15)
    c: Coincident(g10,g14)
    c: Coincident(g13,g14)
    c: Coincident(g12,g16)
    c: Equal(g12,g11)
    c: Equal(g11,g10)
    c: Equal(g10,g13)
    c: Diameter(g13) = 4.2
    c: Distance(g17) = 58.02
    c: Distance(g14) = 181.5
    c: DistanceX(g12) = -1.25
    c: DistanceY(g12) = -8.91
FEATURE [Sketcher::SketchObject] Sketch009  label="Fan003"
  AttachmentOffset = pos=(3,-6,0) rot=(0,0,1;0rad)
  FullyConstrained = true
  MapMode = 5
  Placement = pos=(2e-15,3,-6) rot=(0.57735,0.57735,0.57735;2.0944rad)
  Support = -> [YZ_Plane069]
  sketch-geometry (11):
    g0: LineSegment StartX=173.5 StartY=41.6 StartZ=0 EndX=133.5 EndY=41.6 EndZ=0
    g1: LineSegment StartX=133.5 StartY=41.6 StartZ=0 EndX=133.5 EndY=1.6 EndZ=0
    g2: LineSegment StartX=133.5 StartY=1.6 StartZ=0 EndX=173.5 EndY=1.6 EndZ=0
    g3: LineSegment StartX=173.5 StartY=1.6 StartZ=0 EndX=173.5 EndY=41.6 EndZ=0
    g4: Circle CenterX=173.5 CenterY=41.6 CenterZ=0 NormalX=0 NormalY=0 NormalZ=1 AngleXU=0 Radius=2
    g5: Circle CenterX=133.5 CenterY=41.6 CenterZ=0 NormalX=0 NormalY=0 NormalZ=1 AngleXU=0 Radius=2
    g6: Circle CenterX=133.5 CenterY=1.6 CenterZ=0 NormalX=0 NormalY=0 NormalZ=1 AngleXU=0 Radius=2
    g7: Circle CenterX=173.5 CenterY=1.6 CenterZ=0 NormalX=0 NormalY=0 NormalZ=1 AngleXU=0 Radius=2
    g8: Circle CenterX=153.5 CenterY=21.6 CenterZ=0 NormalX=0 NormalY=0 NormalZ=1 AngleXU=0 Radius=24
    g9: LineSegment StartX=153.5 StartY=21.6 StartZ=0 EndX=153.5 EndY=41.6 EndZ=0
    g10: LineSegment StartX=153.5 StartY=21.6 StartZ=0 EndX=153.5 EndY=1.6 EndZ=0
  constraints (28):
    c: Coincident(g0,g1)
    c: Coincident(g1,g2)
    c: Coincident(g2,g3)
    c: Coincident(g3,g0)
    c: Horizontal(g0)
    c: Horizontal(g2)
    c: Vertical(g1)
    c: Vertical(g3)
    c: Equal(g1,g2)
    c: Coincident(g4,g0)
    c: Coincident(g5,g0)
    c: Coincident(g6,g1)
    c: Coincident(g7,g2)
    c: Equal(g7,g6)
    c: Equal(g6,g5)
    c: Equal(g5,g4)
    c: Diameter(g6) = 4
    c: Coincident(g9,g8)
    c: Vertical(g9)
    c: Symmetric(g5,g4,g9)
    c: Diameter(g8) = 48
    c: Coincident(g10,g8)
    c: PointOnObject(g10,g2)
    c: Vertical(g10)
    c: Equal(g10,g9)
    c: Distance(g0) = 40
    c: DistanceX(g7) = 173.5
    c: DistanceY(g7) = 1.6
FEATURE [Sketcher::SketchObject] Sketch010  label="Analog cutouts"
  FullyConstrained = true
  MapMode = 5
  Placement = pos=(0,0,0) rot=(0.57735,0.57735,0.57735;2.0944rad)
  Support = -> [YZ_Plane069]
  sketch-geometry (36):
    g0: Circle CenterX=121.17 CenterY=7 CenterZ=0 NormalX=0 NormalY=0 NormalZ=1 AngleXU=0 Radius=6
    g1: Circle CenterX=102.17 CenterY=7 CenterZ=0 NormalX=0 NormalY=0 NormalZ=1 AngleXU=0 Radius=6
    g2: LineSegment StartX=138.28 StartY=9.5 StartZ=0 EndX=127.88 EndY=9.5 EndZ=0
    g3: LineSegment StartX=127.88 StartY=9.5 StartZ=0 EndX=127.88 EndY=1 EndZ=0
    g4: LineSegment StartX=127.88 StartY=1 StartZ=0 EndX=138.28 EndY=1 EndZ=0
    g5: LineSegment StartX=138.28 StartY=1 StartZ=0 EndX=138.28 EndY=9.5 EndZ=0
    g6: LineSegment StartX=127.88 StartY=1 StartZ=0 EndX=121.17 EndY=1 EndZ=0
    g7: ArcOfCircle CenterX=172 CenterY=47.45 CenterZ=0 NormalX=0 NormalY=0 NormalZ=1 AngleXU=0 Radius=2.5 StartAngle=5.07e-14 EndAngle=3.14159
    g8: ArcOfCircle CenterX=172 CenterY=-7.55 CenterZ=0 NormalX=0 NormalY=0 NormalZ=1 AngleXU=0 Radius=2.5 StartAngle=3.14159 EndAngle=6.28319
    g9: LineSegment StartX=169.5 StartY=47.45 StartZ=0 EndX=169.5 EndY=-7.55 EndZ=0
    g10: LineSegment StartX=174.5 StartY=-7.55 StartZ=0 EndX=174.5 EndY=47.45 EndZ=0
    g11: ArcOfCircle CenterX=166 CenterY=47.45 CenterZ=0 NormalX=0 NormalY=0 NormalZ=1 AngleXU=0 Radius=2.5 StartAngle=-9.95e-14 EndAngle=3.14159
    g12: ArcOfCircle CenterX=166 CenterY=-7.55 CenterZ=0 NormalX=0 NormalY=0 NormalZ=1 AngleXU=0 Radius=2.5 StartAngle=3.14159 EndAngle=6.28319
    g13: LineSegment StartX=163.5 StartY=47.45 StartZ=0 EndX=163.5 EndY=-7.55 EndZ=0
    g14: LineSegment StartX=168.5 StartY=-7.55 StartZ=0 EndX=168.5 EndY=47.45 EndZ=0
    g15: ArcOfCircle CenterX=160 CenterY=47.45 CenterZ=0 NormalX=0 NormalY=0 NormalZ=1 AngleXU=0 Radius=2.5 StartAngle=-9.33e-14 EndAngle=3.14159
    g16: ArcOfCircle CenterX=160 CenterY=-7.55 CenterZ=0 NormalX=0 NormalY=0 NormalZ=1 AngleXU=0 Radius=2.5 StartAngle=3.14159 EndAngle=6.28319
    g17: LineSegment StartX=157.5 StartY=47.45 StartZ=0 EndX=157.5 EndY=-7.55 EndZ=0
    g18: LineSegment StartX=162.5 StartY=-7.55 StartZ=0 EndX=162.5 EndY=47.45 EndZ=0
    g19: ArcOfCircle CenterX=154 CenterY=47.45 CenterZ=0 NormalX=0 NormalY=0 NormalZ=1 AngleXU=0 Radius=2.5 StartAngle=-7.82e-14 EndAngle=3.14159
    g20: ArcOfCircle CenterX=154 CenterY=-7.55 CenterZ=0 NormalX=0 NormalY=0 NormalZ=1 AngleXU=0 Radius=2.5 StartAngle=3.14159 EndAngle=6.28319
    g21: LineSegment StartX=151.5 StartY=47.45 StartZ=0 EndX=151.5 EndY=-7.55 EndZ=0
    g22: LineSegment StartX=156.5 StartY=-7.55 StartZ=0 EndX=156.5 EndY=47.45 EndZ=0
    g23: ArcOfCircle CenterX=148 CenterY=47.45 CenterZ=0 NormalX=0 NormalY=0 NormalZ=1 AngleXU=0 Radius=2.5 StartAngle=-5.6e-14 EndAngle=3.14159
    g24: ArcOfCircle CenterX=148 CenterY=-7.55 CenterZ=0 NormalX=0 NormalY=0 NormalZ=1 AngleXU=0 Radius=2.5 StartAngle=3.14159 EndAngle=6.28319
    g25: LineSegment StartX=145.5 StartY=47.45 StartZ=0 EndX=145.5 EndY=-7.55 EndZ=0
    g26: LineSegment StartX=150.5 StartY=-7.55 StartZ=0 EndX=150.5 EndY=47.45 EndZ=0
    g27: LineSegment StartX=169.5 StartY=47.45 StartZ=0 EndX=168.5 EndY=47.45 EndZ=0
    g28: LineSegment StartX=163.5 StartY=47.45 StartZ=0 EndX=162.5 EndY=47.45 EndZ=0
    g29: LineSegment StartX=157.5 StartY=47.45 StartZ=0 EndX=156.5 EndY=47.45 EndZ=0
    g30: LineSegment StartX=151.5 StartY=47.45 StartZ=0 EndX=150.5 EndY=47.45 EndZ=0
    g31: ArcOfCircle CenterX=142 CenterY=47.45 CenterZ=0 NormalX=0 NormalY=0 NormalZ=1 AngleXU=0 Radius=2.5 StartAngle=-3.02e-14 EndAngle=3.14159
    g32: ArcOfCircle CenterX=142 CenterY=-7.55 CenterZ=0 NormalX=0 NormalY=0 NormalZ=1 AngleXU=0 Radius=2.5 StartAngle=3.14159 EndAngle=6.28319
    g33: LineSegment StartX=139.5 StartY=47.45 StartZ=0 EndX=139.5 EndY=-7.55 EndZ=0
    g34: LineSegment StartX=144.5 StartY=-7.55 StartZ=0 EndX=144.5 EndY=47.45 EndZ=0
    g35: LineSegment StartX=145.5 StartY=47.45 StartZ=0 EndX=144.5 EndY=47.45 EndZ=0
  constraints (90):
    c: Coincident(g2,g3)
    c: Coincident(g3,g4)
    c: Coincident(g4,g5)
    c: Coincident(g5,g2)
    c: Horizontal(g2)
    c: Horizontal(g4)
    c: Vertical(g3)
    c: Vertical(g5)
    c: Horizontal(g0,g1)
    c: Equal(g0,g1)
    c: Diameter(g1) = 12
    c: DistanceX(g2,g2) = 10.4
    c: Distance(g5) = 8.5
    c: DistanceX(g1,g0) = 19
    c: Coincident(g6,g3)
    c: Horizontal(g6)
    c: Tangent(g6,g0) = 1.5708
    c: DistanceY(g-1,g6) = 1
    c: DistanceX(g-1,g1) = 102.17
    c: DistanceX(g6,g6) = 6.71
    c: Tangent(g7,g9) = -1.5708
    c: Tangent(g9,g8) = -1.5708
    c: Tangent(g8,g10) = -1.5708
    c: Tangent(g10,g7) = -1.5708
    c: Equal(g7,g8)
    c: Vertical(g9)
    c: Diameter(g7) = 5
    c: Distance(g10) = 55
    c: DistanceX(g8) = 172
    c: DistanceY(g8) = -7.55
    c: Tangent(g11,g13) = -1.5708
    c: Tangent(g13,g12) = -1.5708
    c: Tangent(g12,g14) = -1.5708
    c: Tangent(g14,g11) = -1.5708
    c: Equal(g11,g12)
    c: Vertical(g13)
    c: Equal(g7,g11)
    c: Equal(g14,g9)
    c: Tangent(g15,g17) = -1.5708
    c: Tangent(g17,g16) = -1.5708
    c: Tangent(g16,g18) = -1.5708
    c: Tangent(g18,g15) = -1.5708
    c: Equal(g15,g16)
    c: Vertical(g17)
    c: Tangent(g19,g21) = -1.5708
    c: Tangent(g21,g20) = -1.5708
    c: Tangent(g20,g22) = -1.5708
    c: Tangent(g22,g19) = -1.5708
    c: Equal(g19,g20)
    c: Vertical(g21)
    c: Equal(g7,g15)
    c: Equal(g7,g19)
    c: Equal(g18,g9)
    c: Equal(g22,g9)
    c: Horizontal(g15,g11)
    c: Horizontal(g11,g7)
    c: Horizontal(g19,g15)
    c: Tangent(g23,g25) = -1.5708
    c: Tangent(g25,g24) = -1.5708
    c: Tangent(g24,g26) = -1.5708
    c: Tangent(g26,g23) = -1.5708
    c: Equal(g23,g24)
    c: Vertical(g25)
    c: Equal(g7,g23)
    c: Equal(g26,g9)
    c: Horizontal(g19,g23)
    c: Coincident(g27,g7)
    c: Coincident(g27,g11)
    c: Coincident(g28,g11)
    c: Coincident(g28,g15)
    c: Coincident(g29,g15)
    c: Coincident(g29,g19)
    c: Coincident(g30,g19)
    c: Coincident(g30,g23)
    c: Equal(g27,g28)
    c: Equal(g28,g29)
    c: Equal(g29,g30)
    c: Distance(g30) = 1
    c: Tangent(g31,g33) = -1.5708
    c: Tangent(g33,g32) = -1.5708
    c: Tangent(g32,g34) = -1.5708
    c: Tangent(g34,g31) = -1.5708
    c: Equal(g31,g32)
    c: Vertical(g33)
    c: Equal(g7,g31)
    c: Equal(g34,g9)
    c: Horizontal(g31,g23)
    c: Coincident(g35,g23)
    c: Coincident(g35,g31)
    c: Equal(g35,g30)
FEATURE [PartDesign::Pad] Pad004
  Direction = (1,-2e-16,3e-16)
  Length = 1.63
  Length2 = 10
  Placement = pos=(0,0,0) rot=(0.57735,0.57735,0.57735;2.0944rad)
  Profile = -> Sketch007
  ReferenceAxis = -> Sketch007 [N_Axis]
  Reversed = true
  Type = 0
FEATURE [PartDesign::Chamfer] Chamfer
  Angle = 45
  Base = -> Pad004 [Edge33,Edge36,Edge30,Edge27]
  BaseFeature = -> Pad004
  ChamferType = 0
  FlipDirection = false
  Placement = pos=(0,0,0) rot=(0.57735,0.57735,0.57735;2.0944rad)
  Size = 1.6
  Size2 = 1
  SupportTransform = false
  UseAllEdges = false
FEATURE [PartDesign::Pocket] Pocket003
  BaseFeature = -> Chamfer
  Direction = (-1,2e-16,-3e-16)
  Length = 5
  Length2 = 5
  Placement = pos=(0,0,0) rot=(0.57735,0.57735,0.57735;2.0944rad)
  Profile = -> Sketch010
  ReferenceAxis = -> Sketch010 [N_Axis]
  Type = 0
FEATURE [Sketcher::SketchObject] Sketch011
  FullyConstrained = true
  MapMode = 5
  Placement = pos=(0,0,0) rot=(0.57735,0.57735,0.57735;2.0944rad)
  Support = -> [YZ_Plane069]
  sketch-geometry (15):
    g0: Circle CenterX=123.99 CenterY=34.2979 CenterZ=0 NormalX=0 NormalY=0 NormalZ=1 AngleXU=0 Radius=1.75
    g1: Circle CenterX=95.6034 CenterY=33.9737 CenterZ=0 NormalX=0 NormalY=0 NormalZ=1 AngleXU=0 Radius=3.5
    g2: LineSegment StartX=74.79 StartY=42.16 StartZ=0 EndX=14.14 EndY=42.16 EndZ=0
    g3: LineSegment StartX=14.14 StartY=42.16 StartZ=0 EndX=14.14 EndY=-4 EndZ=0
    g4: LineSegment StartX=14.14 StartY=-4 StartZ=0 EndX=74.79 EndY=-4 EndZ=0
    g5: LineSegment StartX=74.79 StartY=-4 StartZ=0 EndX=74.79 EndY=42.16 EndZ=0
    g6: LineSegment StartX=116.776 StartY=42.1588 StartZ=0 EndX=116.776 EndY=30.1588 EndZ=0
    g7: LineSegment StartX=116.776 StartY=30.1588 StartZ=0 EndX=106.776 EndY=30.1588 EndZ=0
    g8: LineSegment StartX=106.776 StartY=30.1588 StartZ=0 EndX=106.776 EndY=42.1588 EndZ=0
    g9: LineSegment StartX=106.776 StartY=42.1588 StartZ=0 EndX=107.776 EndY=42.1588 EndZ=0
    g10: LineSegment StartX=107.776 StartY=42.1588 StartZ=0 EndX=107.776 EndY=31.1588 EndZ=0
    g11: LineSegment StartX=107.776 StartY=31.1588 StartZ=0 EndX=115.776 EndY=31.1588 EndZ=0
    g12: LineSegment StartX=115.776 StartY=31.1588 StartZ=0 EndX=115.776 EndY=42.1588 EndZ=0
    g13: LineSegment StartX=115.776 StartY=42.1588 StartZ=0 EndX=116.776 EndY=42.1588 EndZ=0
    g14: LineSegment StartX=115.776 StartY=31.1588 StartZ=0 EndX=115.776 EndY=30.1588 EndZ=0
  constraints (45):
    c: Coincident(g2,g3)
    c: Coincident(g3,g4)
    c: Coincident(g4,g5)
    c: Coincident(g5,g2)
    c: Horizontal(g2)
    c: Horizontal(g4)
    c: Vertical(g3)
    c: Vertical(g5)
    c: Vertical(g6)
    c: Coincident(g6,g7)
    c: Horizontal(g7)
    c: Coincident(g7,g8)
    c: Vertical(g8)
    c: Coincident(g8,g9)
    c: Horizontal(g9)
    c: Coincident(g9,g10)
    c: Vertical(g10)
    c: Coincident(g10,g11)
    c: Horizontal(g11)
    c: Coincident(g11,g12)
    c: Vertical(g12)
    c: Coincident(g12,g13)
    c: Coincident(g13,g6)
    c: Horizontal(g13)
    c: Horizontal(g12,g9)
    c: Equal(g13,g9)
    c: Distance(g9) = 1
    c: Coincident(g14,g11)
    c: PointOnObject(g14,g7)
    c: Vertical(g14)
    c: Equal(g14,g13)
    c: Distance(g9,g12) = 8
    c: Distance(g8) = 12
    c: DistanceX(g1) = 95.6034
    c: DistanceY(g1) = 33.9737
    c: DistanceX(g0) = 123.99
    c: DistanceY(g0) = 34.2979
    c: DistanceX(g7) = 106.776
    c: DistanceY(g7) = 30.1588
    c: Diameter(g1) = 7
    c: Diameter(g0) = 3.5
    c: DistanceX(g3) = 14.14
    c: DistanceY(g3) = -4
    c: Distance(g5) = 46.16
    c: Distance(g2) = 60.65
FEATURE [Sketcher::SketchObject] Sketch012
  FullyConstrained = true
  MapMode = 5
  Placement = pos=(0,0,0) rot=(0.57735,0.57735,0.57735;2.0944rad)
  Support = -> [YZ_Plane069]
  sketch-geometry (12):
    g0: Circle CenterX=120.903 CenterY=41.7901 CenterZ=0 NormalX=0 NormalY=0 NormalZ=1 AngleXU=0 Radius=1.45
    g1: Circle CenterX=120.903 CenterY=26.7901 CenterZ=0 NormalX=0 NormalY=0 NormalZ=1 AngleXU=0 Radius=1.45
    g2: Circle CenterX=78.9035 CenterY=41.7901 CenterZ=0 NormalX=0 NormalY=0 NormalZ=1 AngleXU=0 Radius=1.45
    g3: Circle CenterX=3.90349 CenterY=41.7901 CenterZ=0 NormalX=0 NormalY=0 NormalZ=1 AngleXU=0 Radius=1.45
    g4: Circle CenterX=3.90349 CenterY=-3.20994 CenterZ=0 NormalX=0 NormalY=0 NormalZ=1 AngleXU=0 Radius=1.45
    g5: Circle CenterX=78.9035 CenterY=-3.20994 CenterZ=0 NormalX=0 NormalY=0 NormalZ=1 AngleXU=0 Radius=1.45
    g6: Circle CenterX=3.90349 CenterY=-3.20994 CenterZ=0 NormalX=0 NormalY=0 NormalZ=1 AngleXU=0 Radius=3
    g7: Circle CenterX=3.90349 CenterY=41.7901 CenterZ=0 NormalX=0 NormalY=0 NormalZ=1 AngleXU=0 Radius=3
    g8: Circle CenterX=78.9035 CenterY=41.7901 CenterZ=0 NormalX=0 NormalY=0 NormalZ=1 AngleXU=0 Radius=3
    g9: Circle CenterX=120.903 CenterY=41.7901 CenterZ=0 NormalX=0 NormalY=0 NormalZ=1 AngleXU=0 Radius=3
    g10: Circle CenterX=120.903 CenterY=26.7901 CenterZ=0 NormalX=0 NormalY=0 NormalZ=1 AngleXU=0 Radius=3
    g11: Circle CenterX=78.9035 CenterY=-3.20994 CenterZ=0 NormalX=0 NormalY=0 NormalZ=1 AngleXU=0 Radius=3
  constraints (30):
    c: Horizontal(g0,g2)
    c: Horizontal(g2,g3)
    c: Horizontal(g5,g4)
    c: Vertical(g5,g2)
    c: Vertical(g1,g0)
    c: Vertical(g4,g3)
    c: Equal(g4,g3)
    c: Equal(g3,g2)
    c: Equal(g2,g5)
    c: Equal(g5,g1)
    c: Equal(g1,g0)
    c: Distance(g0,g1) = 15
    c: Distance(g0,g2) = 42
    c: DistanceX(g3,g2) = 75
    c: DistanceY(g4,g3) = 45
    c: Diameter(g5) = 2.9
    c: DistanceX(g4) = 3.90349
    c: DistanceY(g4) = -3.20994
    c: Coincident(g6,g4)
    c: Coincident(g7,g3)
    c: Coincident(g8,g2)
    c: Coincident(g9,g0)
    c: Coincident(g10,g1)
    c: Coincident(g11,g5)
    c: Diameter(g11) = 6
    c: Equal(g11,g10)
    c: Equal(g10,g9)
    c: Equal(g9,g8)
    c: Equal(g8,g7)
    c: Equal(g7,g6)
FEATURE [PartDesign::Pad] Pad005
  BaseFeature = -> Pocket003
  Direction = (1,-2e-16,3e-16)
  Length = 4.5
  Length2 = 10
  Placement = pos=(0,0,0) rot=(0.57735,0.57735,0.57735;2.0944rad)
  Profile = -> Sketch012
  ReferenceAxis = -> Sketch012 [N_Axis]
  Type = 0
FEATURE [PartDesign::Pocket] Pocket004
  BaseFeature = -> Pad005
  Direction = (-1,2e-16,-3e-16)
  Length = 15
  Length2 = 5
  Midplane = true
  Placement = pos=(0,0,0) rot=(0.57735,0.57735,0.57735;2.0944rad)
  Profile = -> Sketch011
  ReferenceAxis = -> Sketch011 [N_Axis]
  Type = 0
FEATURE [PartDesign::Chamfer] Chamfer001
  Angle = 45
  Base = -> Pocket004 [Edge78,Edge75,Edge76,Edge77]
  BaseFeature = -> Pocket004
  ChamferType = 0
  FlipDirection = false
  Placement = pos=(0,0,0) rot=(0.57735,0.57735,0.57735;2.0944rad)
  Size = 1
  Size2 = 1
  SupportTransform = false
  UseAllEdges = false
FEATURE [Sketcher::SketchObject] Sketch013
  FullyConstrained = true
  MapMode = 5
  Placement = pos=(0,0,0) rot=(0.57735,0.57735,0.57735;2.0944rad)
  Support = -> [YZ_Plane069]
  sketch-geometry (4):
    g0: LineSegment StartX=76.75 StartY=45.9 StartZ=0 EndX=6.25 EndY=45.9 EndZ=0
    g1: LineSegment StartX=6.25 StartY=45.9 StartZ=0 EndX=6.25 EndY=-7.1 EndZ=0
    g2: LineSegment StartX=6.25 StartY=-7.1 StartZ=0 EndX=76.75 EndY=-7.1 EndZ=0
    g3: LineSegment StartX=76.75 StartY=-7.1 StartZ=0 EndX=76.75 EndY=45.9 EndZ=0
  constraints (12):
    c: Coincident(g0,g1)
    c: Coincident(g1,g2)
    c: Coincident(g2,g3)
    c: Coincident(g3,g0)
    c: Horizontal(g0)
    c: Horizontal(g2)
    c: Vertical(g1)
    c: Vertical(g3)
    c: DistanceX(g1) = 6.25
    c: DistanceY(g1) = -7.1
    c: DistanceX(g2,g2) = 70.5
    c: DistanceY(g3,g3) = 53
FEATURE [PartDesign::Pocket] Pocket005
  BaseFeature = -> Chamfer001
  Direction = (-1,2e-16,-3e-16)
  Length = 5
  Length2 = 5
  Placement = pos=(0,0,0) rot=(0.57735,0.57735,0.57735;2.0944rad)
  Profile = -> Sketch013
  ReferenceAxis = -> Sketch013 [N_Axis]
  Reversed = true
  Type = 0
FEATURE [PartDesign::Pad] Pad006
  BaseFeature = -> Pocket005
  Direction = (1,-2e-16,1.2e-15)
  Length = 12.5
  Length2 = 10
  Placement = pos=(0,0,0) rot=(0.57735,0.57735,0.57735;2.0944rad)
  Profile = -> Pocket005 [Face89]
  Type = 0
FEATURE [PartDesign::Pad] Pad007
  BaseFeature = -> Pad006
  Direction = (1,-2e-16,1.6e-15)
  Length = 12.5
  Length2 = 10
  Placement = pos=(0,0,0) rot=(0.57735,0.57735,0.57735;2.0944rad)
  Profile = -> Pad006 [Face88]
  Type = 0
FEATURE [Sketcher::SketchObject] Sketch014
  FullyConstrained = true
  MapMode = 5
  Placement = pos=(0,0,0) rot=(0.57735,0.57735,0.57735;2.0944rad)
  Support = -> [YZ_Plane069]
  sketch-geometry (8):
    g0: LineSegment StartX=84 StartY=-5 StartZ=0 EndX=97 EndY=-5 EndZ=0
    g1: LineSegment StartX=97 StartY=-5 StartZ=0 EndX=97 EndY=-7.5 EndZ=0
    g2: LineSegment StartX=97 StartY=-7.5 StartZ=0 EndX=84 EndY=-7.5 EndZ=0
    g3: LineSegment StartX=84 StartY=-7.5 StartZ=0 EndX=84 EndY=-5 EndZ=0
    g4: LineSegment StartX=177 StartY=-5 StartZ=0 EndX=169 EndY=-5 EndZ=0
    g5: LineSegment StartX=169 StartY=-5 StartZ=0 EndX=169 EndY=-7.5 EndZ=0
    g6: LineSegment StartX=169 StartY=-7.5 StartZ=0 EndX=177 EndY=-7.5 EndZ=0
    g7: LineSegment StartX=177 StartY=-7.5 StartZ=0 EndX=177 EndY=-5 EndZ=0
  constraints (24):
    c: Coincident(g0,g1)
    c: Coincident(g1,g2)
    c: Coincident(g2,g3)
    c: Coincident(g3,g0)
    c: Horizontal(g0)
    c: Horizontal(g2)
    c: Vertical(g1)
    c: Vertical(g3)
    c: DistanceY(g3,g3) = 2.5
    c: DistanceX(g2,g2) = 13
    c: Coincident(g4,g5)
    c: Coincident(g5,g6)
    c: Coincident(g6,g7)
    c: Coincident(g7,g4)
    c: Horizontal(g4)
    c: Horizontal(g6)
    c: Vertical(g5)
    c: Vertical(g7)
    c: Horizontal(g0,g4)
    c: Equal(g5,g1)
    c: DistanceX(g4) = 177
    c: DistanceY(g4) = -5
    c: DistanceX(g-1,g0) = 84
    c: DistanceX(g6,g6) = 8
FEATURE [PartDesign::Pad] Pad008
  BaseFeature = -> Pad007
  Direction = (1,-2e-16,3e-16)
  Length = 17
  Length2 = 10
  Placement = pos=(0,0,0) rot=(0.57735,0.57735,0.57735;2.0944rad)
  Profile = -> Sketch014
  ReferenceAxis = -> Sketch014 [N_Axis]
  Type = 0
FEATURE [Sketcher::SketchObject] Sketch015
  FullyConstrained = true
  MapMode = 5
  Support = -> [XY_Plane069]
  sketch-geometry (2):
    g0: Circle CenterX=11.8 CenterY=173.5 CenterZ=0 NormalX=0 NormalY=0 NormalZ=1 AngleXU=0 Radius=1.6
    g1: Circle CenterX=11.8 CenterY=89.5 CenterZ=0 NormalX=0 NormalY=0 NormalZ=1 AngleXU=0 Radius=1.6
  constraints (6):
    c: Diameter(g0) = 3.2
    c: DistanceX(g0) = 11.8
    c: DistanceY(g0) = 173.5
    c: Equal(g0,g1)
    c: Vertical(g1,g0)
    c: DistanceY(g1,g0) = 84
FEATURE [PartDesign::Pocket] Pocket006
  BaseFeature = -> Pad008
  Direction = (0,0,-1)
  Length = 32
  Length2 = 5
  Midplane = true
  Placement = pos=(0,0,0) rot=(0.57735,0.57735,0.57735;2.0944rad)
  Profile = -> Sketch015
  ReferenceAxis = -> Sketch015 [N_Axis]
  Type = 0
FEATURE [Sketcher::SketchObject] Sketch016
  FullyConstrained = true
  MapMode = 5
  Placement = pos=(0,0,0) rot=(0.57735,0.57735,0.57735;2.0944rad)
  Support = -> [YZ_Plane069]
  sketch-geometry (4):
    g0: LineSegment StartX=169.017 StartY=10 StartZ=0 EndX=169.017 EndY=-11 EndZ=0
    g1: LineSegment StartX=169.017 StartY=-11 StartZ=0 EndX=175.017 EndY=-11 EndZ=0
    g2: LineSegment StartX=175.017 StartY=-11 StartZ=0 EndX=175.017 EndY=10 EndZ=0
    g3: ArcOfCircle CenterX=172.017 CenterY=10 CenterZ=0 NormalX=0 NormalY=0 NormalZ=1 AngleXU=0 Radius=3 StartAngle=3.14159 EndAngle=6.28319
  constraints (13):
    c: Coincident(g0,g1)
    c: Coincident(g1,g2)
    c: Horizontal(g1)
    c: Vertical(g0)
    c: Vertical(g2)
    c: DistanceX(g0,g2) = 6
    c: DistanceX(g0) = 169.017
    c: DistanceY(g1,g-1) = 11
    c: Coincident(g3,g0)
    c: Coincident(g3,g2)
    c: Horizontal(g2,g3)
    c: Equal(g2,g0)
    c: DistanceY(g2,g2) = 21
FEATURE [PartDesign::Pad] Pad009
  BaseFeature = -> Pocket006
  Direction = (1,-2e-16,3e-16)
  Length = 10
  Length2 = 10
  Placement = pos=(0,0,0) rot=(0.57735,0.57735,0.57735;2.0944rad)
  Profile = -> Sketch016
  ReferenceAxis = -> Sketch016 [N_Axis]
  Reversed = true
  Type = 3
  UpToFace = -> Pocket006 [Face1]
FEATURE [Sketcher::SketchObject] Sketch017
  ExternalGeometry = -> [Pad009]
  FullyConstrained = true
  MapMode = 5
  Placement = pos=(0,0,0) rot=(0.57735,0.57735,0.57735;2.0944rad)
  Support = -> [YZ_Plane069]
  sketch-geometry (7):
    g0: ArcOfCircle CenterX=133 CenterY=-7.55 CenterZ=0 NormalX=0 NormalY=0 NormalZ=1 AngleXU=0 Radius=2.5 StartAngle=4.71239 EndAngle=7.85398
    g1: ArcOfCircle CenterX=100 CenterY=-7.55 CenterZ=0 NormalX=0 NormalY=0 NormalZ=1 AngleXU=0 Radius=2.5 StartAngle=1.5708 EndAngle=4.71239
    g2: LineSegment StartX=133 StartY=-5.05 StartZ=0 EndX=100 EndY=-5.05 EndZ=0
    g3: LineSegment StartX=100 StartY=-10.05 StartZ=0 EndX=133 EndY=-10.05 EndZ=0
    g4: LineSegment StartX=133 StartY=-10.05 StartZ=0 EndX=142 EndY=-10.05 EndZ=0
    g5: Circle CenterX=173.502 CenterY=3.91 CenterZ=0 NormalX=0 NormalY=0 NormalZ=1 AngleXU=0 Radius=1.625
    g6: Circle CenterX=89.5018 CenterY=3.91 CenterZ=0 NormalX=0 NormalY=0 NormalZ=1 AngleXU=0 Radius=1.625
  constraints (18):
    c: Tangent(g0,g2) = -1.5708
    c: Tangent(g2,g1) = -1.5708
    c: Tangent(g1,g3) = -1.5708
    c: Tangent(g3,g0) = -1.5708
    c: Equal(g0,g1)
    c: Horizontal(g2)
    c: Diameter(g0) = 5
    c: Coincident(g4,g0)
    c: Tangent(g4,g-3) = -1.5708
    c: Horizontal(g4)
    c: DistanceX(g3,g3) = 33
    c: DistanceX(g-1,g1) = 100
    c: Equal(g6,g5)
    c: Horizontal(g5,g6)
    c: DistanceX(g6,g5) = 84
    c: Diameter(g6) = 3.25
    c: DistanceX(g6) = 89.5018
    c: DistanceY(g6) = 3.91
FEATURE [PartDesign::Pocket] Pocket007
  BaseFeature = -> Pad009
  Direction = (-1,2e-16,-3e-16)
  Length = 5
  Length2 = 5
  Placement = pos=(0,0,0) rot=(0.57735,0.57735,0.57735;2.0944rad)
  Profile = -> Sketch017
  ReferenceAxis = -> Sketch017 [N_Axis]
  Type = 0
FEATURE [Sketcher::SketchObject] Sketch018
  FullyConstrained = true
  MapMode = 5
  Placement = pos=(0,0,0) rot=(0.57735,0.57735,0.57735;2.0944rad)
  Support = -> [YZ_Plane069]
  sketch-geometry (1):
    g0: Circle CenterX=111.65 CenterY=34.9425 CenterZ=0 NormalX=0 NormalY=0 NormalZ=1 AngleXU=0 Radius=3
  constraints (3):
    c: DistanceX(g0) = 111.65
    c: DistanceY(g0) = 34.9425
    c: Diameter(g0) = 6
FEATURE [PartDesign::Pad] Pad010
  BaseFeature = -> Pocket007
  Direction = (1,-2e-16,3e-16)
  Length = 1
  Length2 = 10
  Placement = pos=(0,0,0) rot=(0.57735,0.57735,0.57735;2.0944rad)
  Profile = -> Sketch018
  ReferenceAxis = -> Sketch018 [N_Axis]
  Type = 0
FEATURE [PartDesign::Body] Body002  label="Front Panel"
  Group = -> [Binder001,Sketch006,Sketch007,Sketch009,Sketch010,Pad004,Chamfer,Pocket003,Sketch011,Sketch012,Pad005,Pocket004,Chamfer001,Sketch013,Pocket005,Pad006,Pad007,Sketch014,Pad008,Sketch015,Pocket006,Sketch016,Pad009,Sketch017,Pocket007,Sketch018,Pad010]
  Origin = -> Origin069
  Placement = pos=(-0.8,0,0) rot=(0,0,1;0rad)
  Tip = -> Pad010
COMPONENT P13 — geometry summary ("1455U2201"; no construction recipe available for this part):
  bounding box: 227.0 x 196.1 x 71.1 mm
  tessellated surface: 43,576 triangles
  volume: 251418 mm^3 (8% of its bounding box)
  symmetry: mirror-symmetric across its y mid-plane
PROVENANCE & LICENSES
A FreeCAD (.FCStd) document from a public repository crawl; recipes are the document's own serialized feature recipes (and, for linked parts, companion documents' recipes).
License: as declared in the source repository (recorded in the dataset sidecar).
